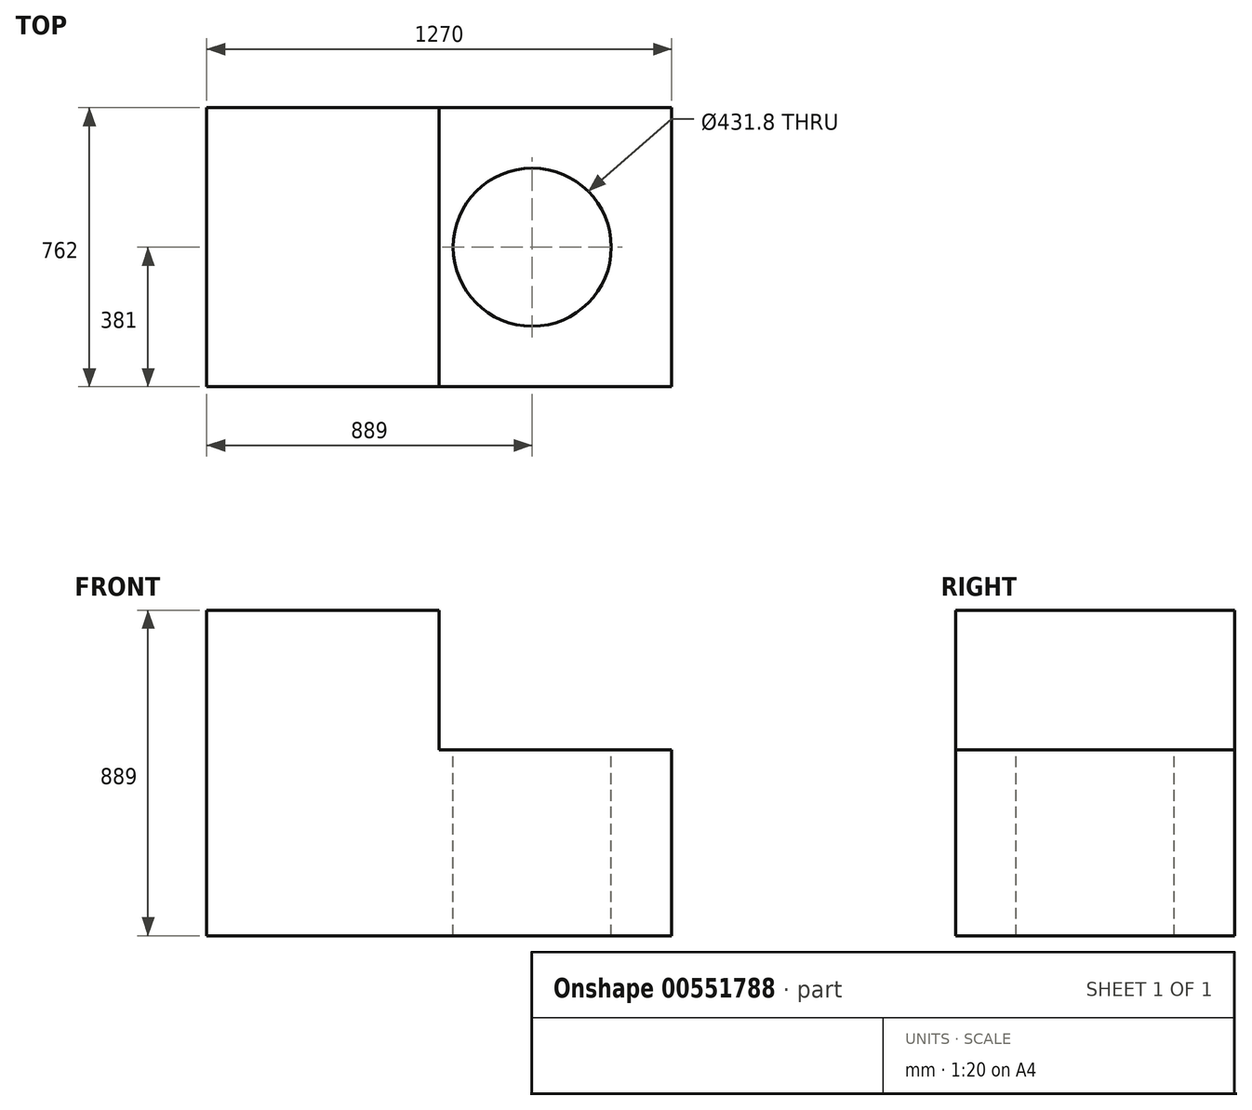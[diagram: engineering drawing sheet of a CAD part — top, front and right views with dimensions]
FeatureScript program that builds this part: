
annotation { "Feature Type Name" : "Feature", "Feature Type Description" : "" }
export const myFeature = defineFeature(function(context is Context, id is Id, definition is map)
    precondition{}
    {
        {
            var Q0;
            Q0=qCreatedBy(makeId("Front.planeOp"),FACE);
            var sketch = newSketch(context, id + "F0", { "sketchPlane" : qUnion([Q0])});
            skLineSegment(sketch, "E0.bottom", {"start": v(0, -448.89) * mm, "end": v(-635, -448.89) * mm});
            skLineSegment(sketch, "E0.top", {"start": v(0, 440.11) * mm, "end": v(-635, 440.11) * mm});
            skLineSegment(sketch, "E0.left", {"start": v(0, 59.11) * mm, "end": v(0, 440.11) * mm});
            skLineSegment(sketch, "E0.right", {"start": v(-635, -448.89) * mm, "end": v(-635, 440.11) * mm});
            skLineSegment(sketch, "E1.bottom", {"start": v(0, -448.89) * mm, "end": v(635, -448.89) * mm});
            skLineSegment(sketch, "E1.top", {"start": v(0, 59.11) * mm, "end": v(635, 59.11) * mm});
            skLineSegment(sketch, "E1.right", {"start": v(635, -448.89) * mm, "end": v(635, 59.11) * mm});
            skSolve(sketch);
        }
        {
            var Q0;
            Q0=makeQuery(id+"F0.imprint","IMPRINT",FACE,{"disambiguationData":[TD([[makeQuery(id+"F0.imprint","IMPRINT",EDGE,{"derivedFrom":sQuery(id+"F0.wireOp",EDGE,"E0.bottom")}),-1.0]])]});
            extrude(context, id + "F1", {"entities" : qUnion([Q0]), "endBound" : BoundingType.SYMMETRIC, "depth" : 762 * mm, "offsetDistance" : 25.4 * mm});
        }
        {
            var Q0;
            Q0=qCreatedBy(makeId("Top.planeOp"),FACE);
            var sketch = newSketch(context, id + "F2", { "sketchPlane" : qUnion([Q0])});
            skCircle(sketch, "E2", {"center": v(254, 0) * mm, "radius": 215.9 * mm});
            skSolve(sketch);
        }
        {
            var Q0;
            Q0=qSketchRegion(id+"F2",true);
            var Q1;
            Q1=makeQuery(id+"F1.opExtrude","SWEPT_FACE",FACE,{"disambiguationData":[OSD([sQuery(id+"F0.wireOp",EDGE,"E1.top")])]});
            extrude(context, id + "F3", {"entities" : qUnion([Q0]), "operationType" : NewBodyOperationType.REMOVE, "endBound" : BoundingType.SYMMETRIC, "oppositeDirection" : true, "depth" : 1016 * mm, "endBoundEntityFace" : qUnion([Q1]), "hasOffset" : true, "offsetDistance" : 533.4 * mm});
        }
    });
